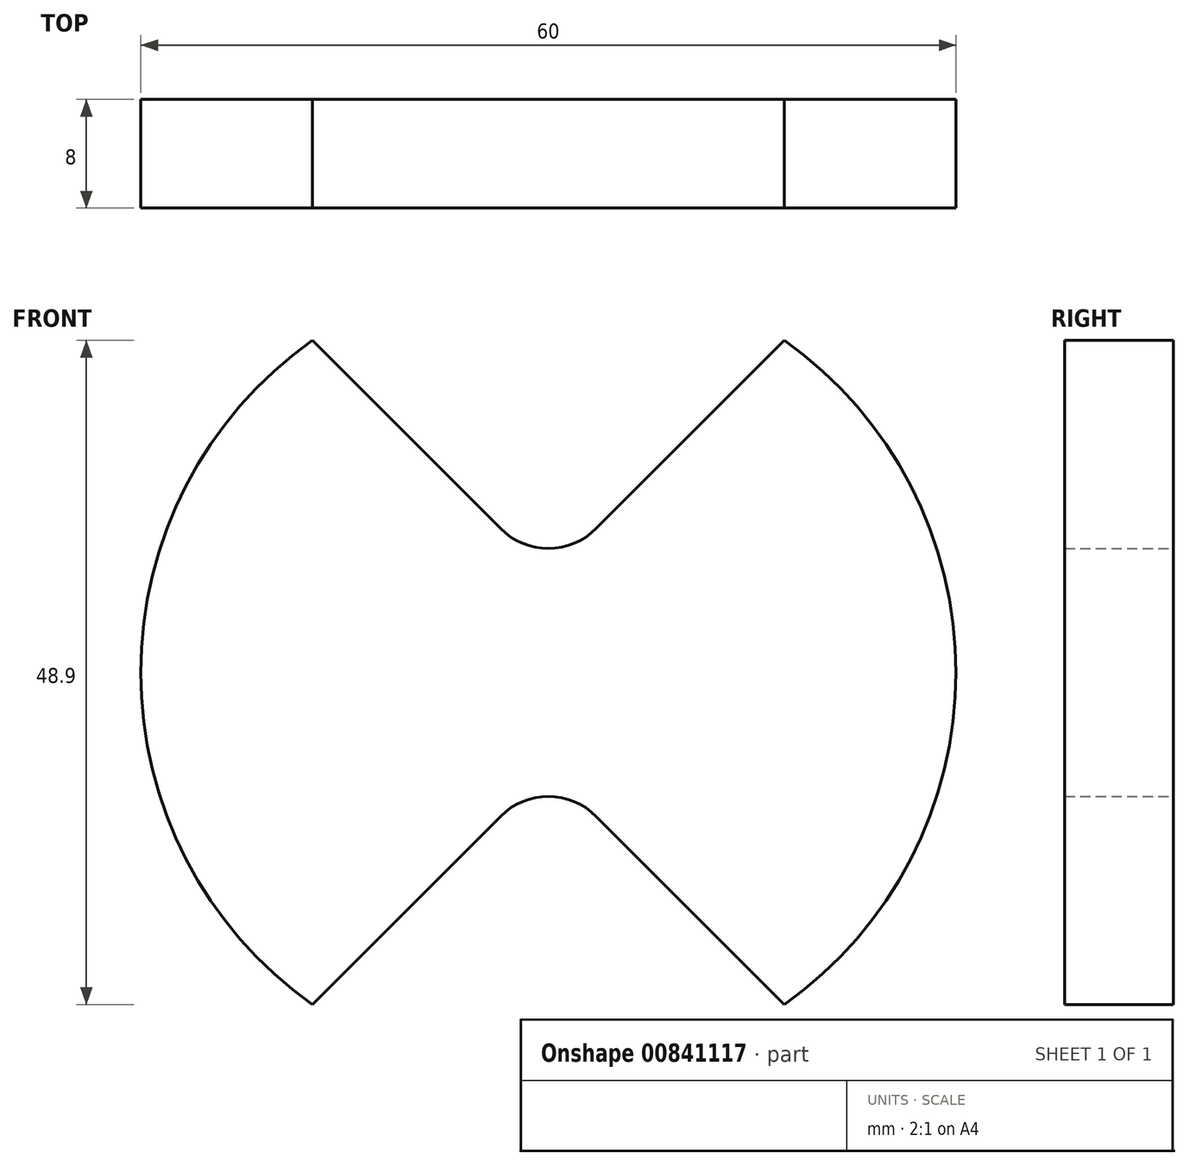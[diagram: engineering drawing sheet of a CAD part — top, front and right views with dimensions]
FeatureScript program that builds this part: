
annotation { "Feature Type Name" : "Feature", "Feature Type Description" : "" }
export const myFeature = defineFeature(function(context is Context, id is Id, definition is map)
    precondition{}
    {
        {
            var Q0;
            Q0=qCreatedBy(makeId("Front.planeOp"),FACE);
            var sketch = newSketch(context, id + "F0", { "sketchPlane" : qUnion([Q0])});
            skCircle(sketch, "E0", {"center": v(0, 0) * mm, "radius": 30 * mm});
            skSolve(sketch);
        }
        {
            var Q0;
            Q0=makeQuery(id+"F0.imprint","IMPRINT",FACE,{"disambiguationData":[TD([[makeQuery(id+"F0.imprint","IMPRINT",EDGE,{"derivedFrom":sQuery(id+"F0.wireOp",EDGE,"E0")}),1.0]])]});
            extrude(context, id + "F1", {"entities" : qUnion([Q0]), "depth" : 8 * mm, "offsetDistance" : 25 * mm});
        }
        {
            var Q0;
            Q0=qCreatedBy(makeId("Front.planeOp"),FACE);
            var sketch = newSketch(context, id + "F2", { "sketchPlane" : qUnion([Q0])});
            skLineSegment(sketch, "E1", {"start": v(0, 0) * mm, "end": v(35.9, 35.9) * mm, "construction": true});
            skLineSegment(sketch, "E2", {"start": v(-35.9, 35.9) * mm, "end": v(0, 0) * mm, "construction": true});
            skLineSegment(sketch, "E3", {"start": v(-35.9, 35.9) * mm, "end": v(35.9, 35.9) * mm, "construction": true});
            skLineSegment(sketch, "E4.0", {"start": v(3.54, 10.6) * mm, "end": v(23.82, 30.9) * mm});
            skLineSegment(sketch, "E4.1", {"start": v(-23.82, 30.9) * mm, "end": v(-3.54, 10.6) * mm});
            skLineSegment(sketch, "E4.2", {"start": v(-23.82, 30.9) * mm, "end": v(23.82, 30.9) * mm});
            skPoint(sketch, "E5.visualSharp", {"position": v(0, 7.07) * mm});
            skArc(sketch, "E5.filletArc", {"start": v(-3.54, 10.6) * mm, "mid": v(0, 9.14) * mm, "end": v(3.54, 10.6) * mm});
            skLineSegment(sketch, "E6.MirrorCS", {"start": v(-35.9, -35.9) * mm, "end": v(0, 0) * mm, "construction": true});
            skLineSegment(sketch, "E7.MirrorCS", {"start": v(0, 0) * mm, "end": v(35.9, -35.9) * mm, "construction": true});
            skLineSegment(sketch, "E8.MirrorCS", {"start": v(-35.9, -35.9) * mm, "end": v(35.9, -35.9) * mm, "construction": true});
            skArc(sketch, "E9.MirrorCS", {"start": v(-3.54, -10.6) * mm, "mid": v(0, -9.14) * mm, "end": v(3.54, -10.6) * mm});
            skLineSegment(sketch, "E10.MirrorCS", {"start": v(-23.82, -30.9) * mm, "end": v(-3.54, -10.6) * mm});
            skLineSegment(sketch, "E11.MirrorCS", {"start": v(-23.82, -30.9) * mm, "end": v(23.82, -30.9) * mm});
            skPoint(sketch, "E12.MirrorP", {"position": v(0, -7.07) * mm});
            skLineSegment(sketch, "E13.MirrorCS", {"start": v(3.54, -10.6) * mm, "end": v(23.82, -30.9) * mm});
            skSolve(sketch);
        }
        {
            var Q0;
            Q0=qCreatedBy(makeId("Front.planeOp"),FACE);
            var sketch = newSketch(context, id + "F3", { "sketchPlane" : qUnion([Q0])});
            skCircle(sketch, "E14", {"center": v(-3.89, 21.16) * mm, "radius": 2.5 * mm});
            skCircle(sketch, "E15.MirrorC", {"center": v(3.89, 21.16) * mm, "radius": 2.5 * mm});
            skCircle(sketch, "E16.MirrorC", {"center": v(3.89, -21.16) * mm, "radius": 2.5 * mm});
            skCircle(sketch, "E17.MirrorC", {"center": v(-3.89, -21.16) * mm, "radius": 2.5 * mm});
            skSolve(sketch);
        }
        {
            var Q0;
            Q0 = qSketchRegion(id + "F2", true);
            extrude(context, id + "F4", {"entities" : qUnion([Q0]), "operationType" : NewBodyOperationType.REMOVE, "depth" : 16.1 * mm, "offsetDistance" : 25 * mm});
        }
    });
